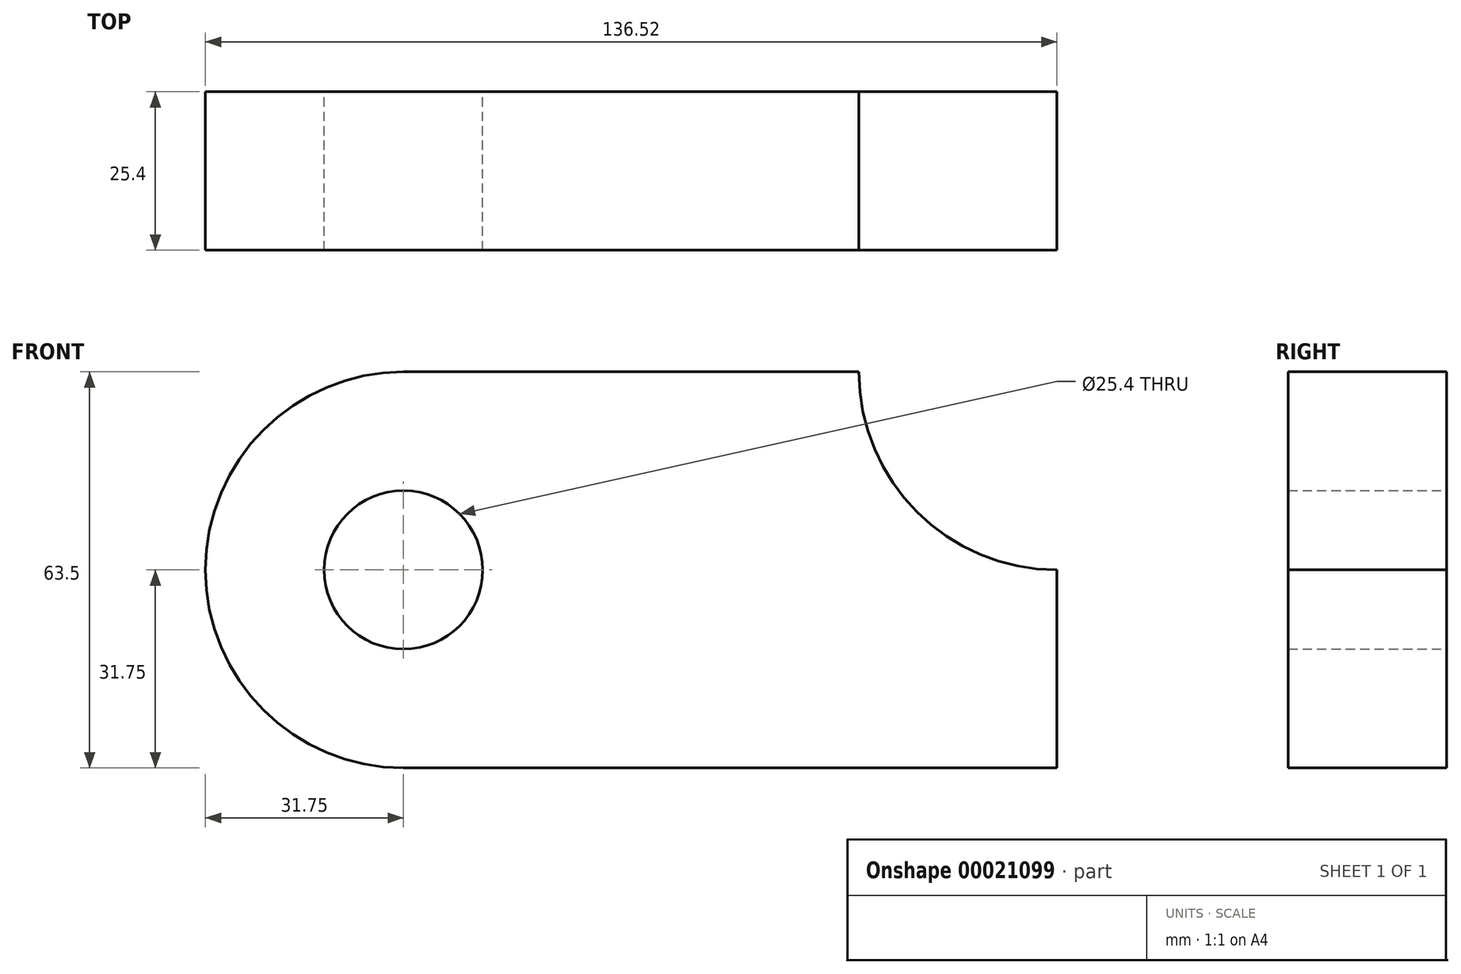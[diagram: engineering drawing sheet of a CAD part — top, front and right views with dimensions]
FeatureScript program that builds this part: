
annotation { "Feature Type Name" : "Feature", "Feature Type Description" : "" }
export const myFeature = defineFeature(function(context is Context, id is Id, definition is map)
    precondition{}
    {
        {
            var Q0;
            Q0=qCreatedBy(makeId("Front.planeOp"),FACE);
            var sketch = newSketch(context, id + "F0", { "sketchPlane" : qUnion([Q0])});
            skLineSegment(sketch, "E0.bottom", {"start": v(0, 0) * mm, "end": v(104.78, 0) * mm});
            skLineSegment(sketch, "E0.top", {"start": v(0, 63.5) * mm, "end": v(73.03, 63.5) * mm});
            skLineSegment(sketch, "E0.right", {"start": v(104.78, 0) * mm, "end": v(104.78, 31.75) * mm});
            skArc(sketch, "E1", {"start": v(0, 63.5) * mm, "mid": v(-31.75, 31.75) * mm, "end": v(0, 0) * mm});
            skCircle(sketch, "E2", {"center": v(0, 31.75) * mm, "radius": 12.7 * mm});
            skArc(sketch, "E3", {"start": v(73.03, 63.5) * mm, "mid": v(82.32, 41.05) * mm, "end": v(104.78, 31.75) * mm});
            skSolve(sketch);
        }
        {
            var Q0;
            Q0=makeQuery(id+"F0.imprint","IMPRINT",FACE,{"disambiguationData":[TD([[makeQuery(id+"F0.imprint","IMPRINT",EDGE,{"derivedFrom":sQuery(id+"F0.wireOp",EDGE,"E0.bottom")}),1.0]])]});
            extrude(context, id + "F1", {"entities" : qUnion([Q0]), "depth" : 25.4 * mm});
        }
    });
